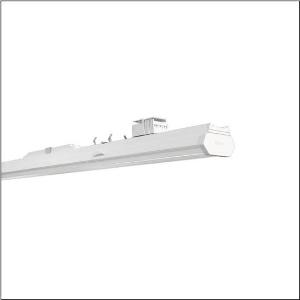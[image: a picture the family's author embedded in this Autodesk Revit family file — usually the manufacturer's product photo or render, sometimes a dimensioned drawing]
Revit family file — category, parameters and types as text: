
# Revit family: licross_21_protected_mo_52td12dn4a5g3s4
name_source: partatom
category: Lighting Fixtures
units: mm (PartAtom-declared; Revit-internal decimal feet)

## family parameters
Cut with Voids When Loaded = No
Host = Face
Light Source = No
Part Type = Normal
Room Calculation Point = No
Round Connector Dimension = Use Diameter
Shared = No

## types (1)
- --- (1 x LED, 940 lm, 6.8 W, 4000K)
    Apparent Load = 7 VA
    CIE Flux Codes = 73 92 98 99 100
    Color Rendering = 80
    Color Temperature = 4000K
    Default Elevation = 1800 mm
    Description = Licross 21 Protected MO, luminaire insert, of sheet steel, galvanised, coil coated, white, length: 1.500mm, width: 90mm, height: 103mm, LED rated luminous flux: 10.700lm, light colour: 840, SDCM (Standard Deviation of Colour Matching)MacAdam ≤ 3 SDCM (initial), control gear: DALI 2, with plug, 6-pole, with phase selection, for trunking rail, 9 or 11-core, mains connection: 220..240V, AC, 50/60Hz, rated input power: 66W, for trunking rail, 9-/11-core, internal wiring halogen-free, for emergency light function, converter,control gear: single battery element, battery: LiFePO4, 9Ah, primary light control with lens, of plastic, primary optical cover: cover, of PMMA, light emission: direct distribution, primary light characteristic: symmetric, protection rating (complete): IP54, insulation class (complete): insulation class I (protective earthing), certification: CE, UKCA, protection symbol: D if used in an environment with non-conductive dust loads with corresponding accessories, impact resistance: IK06, permissible ambient temperature for indoor applications: +5..+35°C, standard: EN 60598-2-22, LABS conformity tested according to VDMA 24364:2018-05, reducing of maximum allowable ambient temperature of 5°C with ceiling mounting, corresponds to IFS (International Featured Standards) requirements for safety and quality in the food industry, The light source and the operating device comply with the requirements of the Ecodesign Regulation (EU) 2019/2020 and are replaceable in accordance with this regulation, packaging unit: 1 piece
    Height = 92 mm
    Lamp = 1 x LED
    Lamp Light Flux = 940 lm
    Lamp Power = 6.8 W
    Lamp count = 1
    Length = 1500 mm
    Luminous efficacy = 138 lm/W
    Manufacturer = Siteco
    ModVariant = No
    Model = 52TD12DN4A5G3S4
    Mounting Place = Ceiling
    Mounting Type = Pendant
    Number of Poles = 1
    OnlyDefault = Yes
    Power Factor = 1
    Product Name = Licross 21 Protected MO
    Product group = luminaire insert | ceiling pendant
    ProductGroupID = 901
    Protection Class = Protection class I
    Protection Degree = IP 54
    RLX_Detail_Level = 1
    RLX_Emergency_Light_Flux = 0 lm
    RLX_Emergency_Type = 0
    RLX_Emergency_Type_DB = No
    RlxData = <blob elided: 25073 chars, md5=b2e7aaf8>
    Socket = socket
    Standby Power = 0 W
    System Light Flux = 940 lm
    System Power = 7 W
    Type Comments = : emergency light operation: 3 h
    Type Image = l_1256148.jpg
    URL = http://relux.com
    VarID = @adj_112431
    Voltage = 0 V
    Weight = 0.00 kg
    Width = 88 mm

## geometry (parser evidence)
native form markers: Blend x4, Sweep x9
no freeform markers — native parametric forms only
